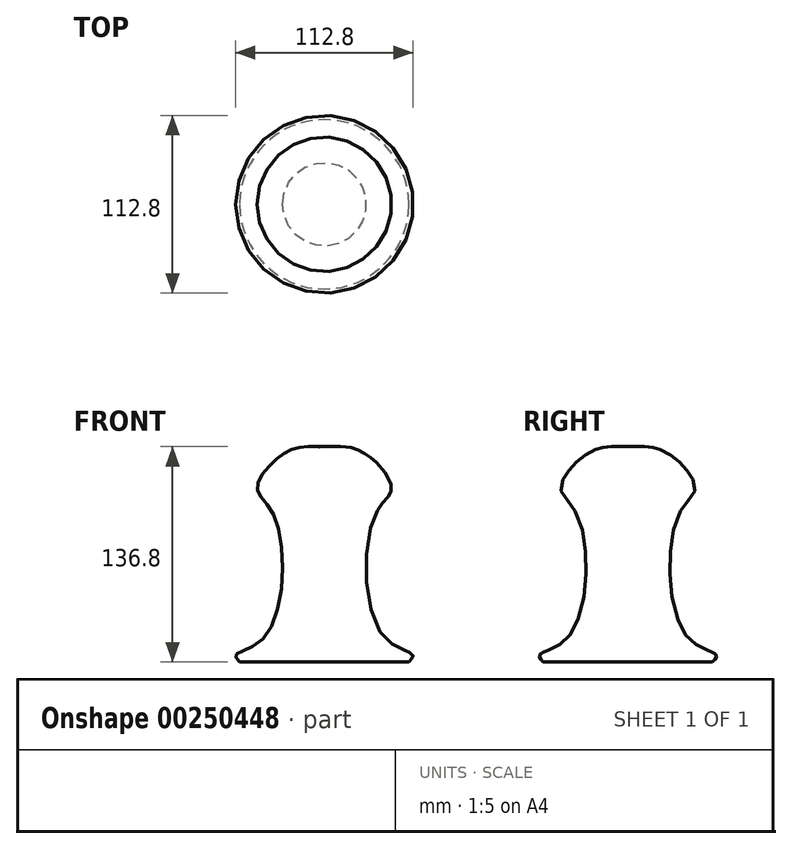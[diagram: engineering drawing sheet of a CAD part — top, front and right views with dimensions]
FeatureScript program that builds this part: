
annotation { "Feature Type Name" : "Feature", "Feature Type Description" : "" }
export const myFeature = defineFeature(function(context is Context, id is Id, definition is map)
    precondition{}
    {
        {
            var Q0;
            Q0=qCreatedBy(makeId("Front.planeOp"),FACE);
            var sketch = newSketch(context, id + "F0", { "sketchPlane" : qUnion([Q0])});
            skLineSegment(sketch, "E0", {"start": v(0, -75.15) * mm, "end": v(0, 128.05) * mm});
            skLineSegment(sketch, "E1", {"start": v(0, -75.15) * mm, "end": v(-63.5, -75.15) * mm});
            skLineSegment(sketch, "E2", {"start": v(-63.5, -75.15) * mm, "end": v(-63.5, -68.8) * mm});
            skLineSegment(sketch, "E3", {"start": v(-63.5, -68.8) * mm, "end": v(-56.27, -63.47) * mm});
            skLineSegment(sketch, "E4", {"start": v(-56.27, -63.47) * mm, "end": v(-56.27, -59.87) * mm});
            skLineSegment(sketch, "E5", {"start": v(-56.27, -59.87) * mm, "end": v(-53.78, -59.87) * mm});
            skFitSpline(sketch, "E6", {"points": [v(-53.78, -59.87) * mm, v(-56.27, -55.44) * mm, v(-37.44, -43.53) * mm, v(-31.62, 32.36) * mm, v(-42.7, 50.08) * mm, v(-32.18, 67.53) * mm, v(-16.4, 76.4) * mm, v(0, 76.12) * mm], "startDerivative": vector(-67.88, 70.74) * mm, "endDerivative": vector(136.72, -16.07) * mm});
            skSolve(sketch);
        }
        {
            var Q0;
            Q0=sQuery(id+"F0.wireOp",EDGE,"E6");
            var Q1;
            Q1=sQuery(id+"F0.wireOp",EDGE,"E0");
            revolve(context, id + "F1", {"bodyType" : ToolBodyType.SURFACE, "surfaceEntities" : qUnion([Q0]), "axis" : qUnion([Q1]), "revolveType" : RevolveType.FULL});
        }
    });
